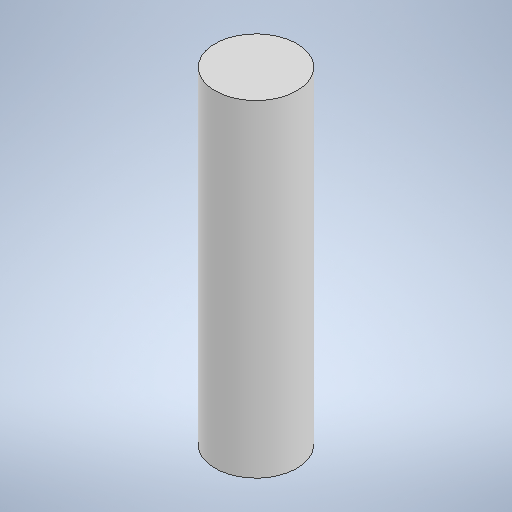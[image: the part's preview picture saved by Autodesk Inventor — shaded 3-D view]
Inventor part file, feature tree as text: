
AUTODESK INVENTOR PART (.ipt)
format: ipt  version: 2025.1 (Build 291241000, 241)  size: 226,304 bytes
history: native  units: mm
features: extrude x1, sketch x1
ambient origin geometry x8: Origin, YZ Plane, XZ Plane, XY Plane, X Axis, Y Axis, Z Axis, Center Point
bodies: Solid1 (feature_tree)
feature tree (2):
  extrude  "Extrusion1"  Depth=16.0mm TaperAngle=0.0deg
  sketch  "Sketch1"  dims[d0=4.0mm d1=16.0mm d2=0.0mm]
